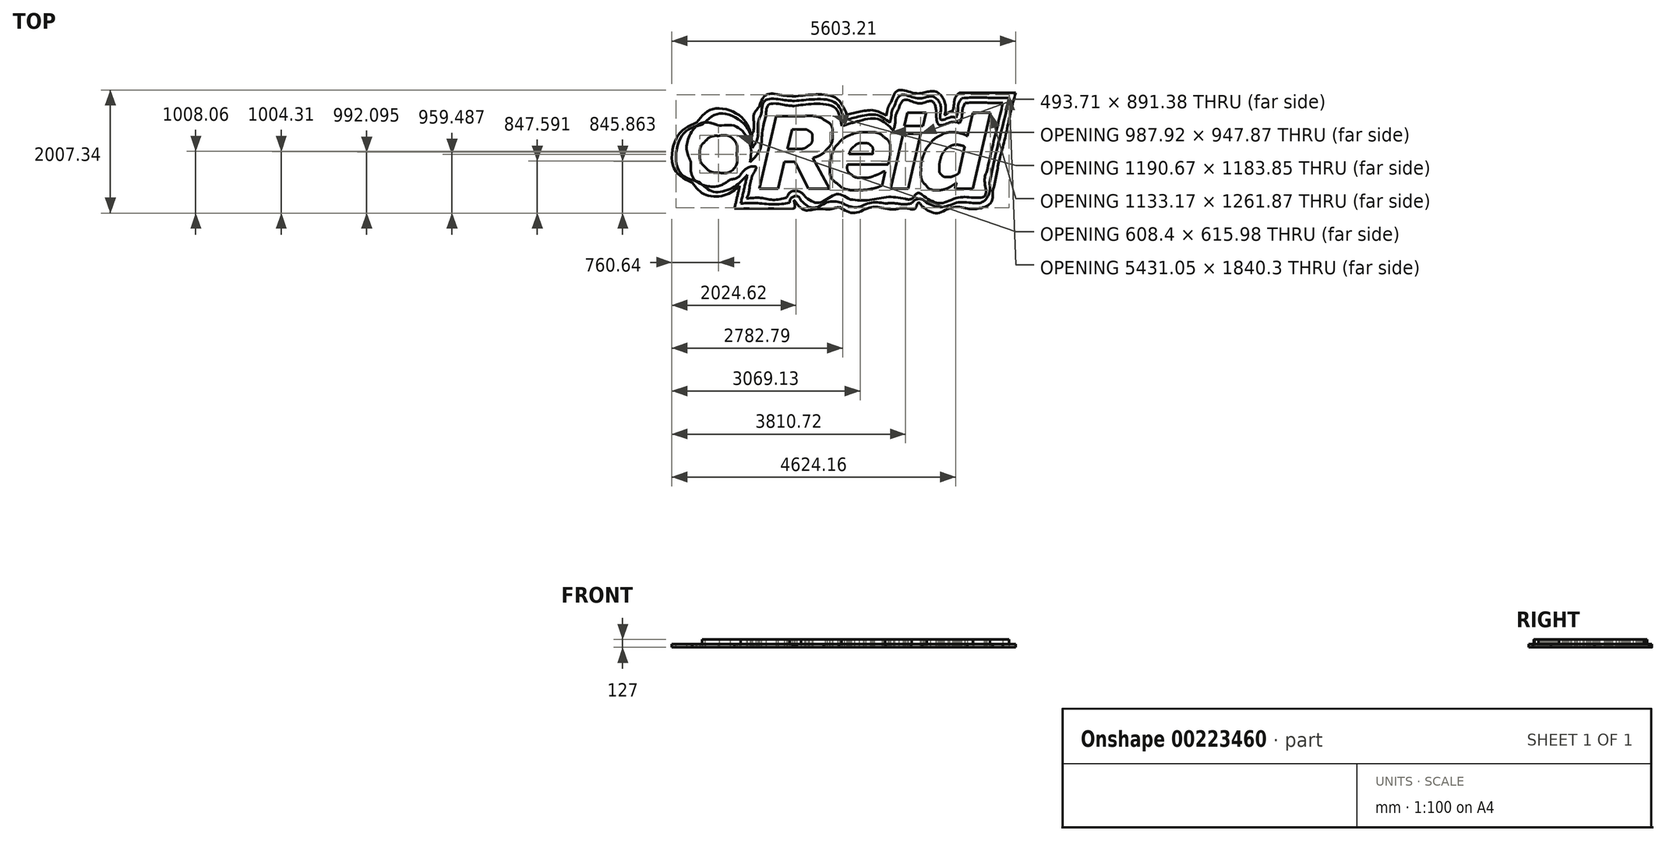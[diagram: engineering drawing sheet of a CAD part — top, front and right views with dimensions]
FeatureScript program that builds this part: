
annotation { "Feature Type Name" : "Feature", "Feature Type Description" : "" }
export const myFeature = defineFeature(function(context is Context, id is Id, definition is map)
    precondition{}
    {
        {
            var Q0;
            Q0=qCreatedBy(makeId("Top.planeOp"),FACE);
            var sketch = newSketch(context, id + "F0", { "sketchPlane" : qUnion([Q0])});
            skFitSpline(sketch, "E0", {"points": [v(-1814.54, -52.81) * mm, v(-1814.54, -217.56) * mm, v(-1948.1, -351.11) * mm, v(-2112.84, -351.11) * mm]});
            skFitSpline(sketch, "E1", {"points": [v(-2112.84, -351.11) * mm, v(-2191.95, -351.11) * mm, v(-2267.83, -319.69) * mm, v(-2323.77, -263.74) * mm]});
            skFitSpline(sketch, "E2", {"points": [v(-2323.77, -263.74) * mm, v(-2379.71, -207.8) * mm, v(-2411.14, -131.93) * mm, v(-2411.14, -52.81) * mm]});
            skFitSpline(sketch, "E3", {"points": [v(-2411.14, -52.81) * mm, v(-2411.14, 26.3) * mm, v(-2379.71, 102.18) * mm, v(-2323.77, 158.12) * mm]});
            skFitSpline(sketch, "E4", {"points": [v(-2323.77, 158.12) * mm, v(-2267.83, 214.06) * mm, v(-2191.95, 245.49) * mm, v(-2112.84, 245.49) * mm]});
            skFitSpline(sketch, "E5", {"points": [v(-2112.84, 245.49) * mm, v(-1948.1, 245.49) * mm, v(-1814.54, 111.93) * mm, v(-1814.54, -52.81) * mm]});
            skFitSpline(sketch, "E6", {"points": [v(1769.4, -519.26) * mm, v(1741.88, -536.72) * mm, v(1717.54, -552.6) * mm, v(1696.37, -566.88) * mm]});
            skFitSpline(sketch, "E7", {"points": [v(1696.37, -566.88) * mm, v(1675.74, -580.64) * mm, v(1652.72, -593.34) * mm, v(1627.32, -604.98) * mm]});
            skFitSpline(sketch, "E8", {"points": [v(1627.32, -604.98) * mm, v(1603.5, -615.57) * mm, v(1579.96, -623.5) * mm, v(1556.67, -628.8) * mm]});
            skFitSpline(sketch, "E9", {"points": [v(1556.67, -628.8) * mm, v(1533.92, -634.09) * mm, v(1506.4, -636.73) * mm, v(1474.12, -636.73) * mm]});
            skFitSpline(sketch, "E10", {"points": [v(1474.12, -636.73) * mm, v(1387.87, -636.73) * mm, v(1318.81, -608.69) * mm, v(1266.95, -552.6) * mm]});
            skFitSpline(sketch, "E11", {"points": [v(1266.95, -552.6) * mm, v(1215.63, -496.5) * mm, v(1189.96, -416.87) * mm, v(1189.96, -313.68) * mm]});
            skFitSpline(sketch, "E12", {"points": [v(1189.96, -313.68) * mm, v(1189.96, -229.01) * mm, v(1203.45, -149.64) * mm, v(1230.44, -75.55) * mm]});
            skFitSpline(sketch, "E13", {"points": [v(1230.44, -75.55) * mm, v(1257.96, -0.94) * mm, v(1295.53, 64.94) * mm, v(1343.15, 122.1) * mm]});
            skFitSpline(sketch, "E14", {"points": [v(1343.15, 122.1) * mm, v(1389.72, 177.65) * mm, v(1444.75, 221.84) * mm, v(1508.25, 254.65) * mm]});
            skFitSpline(sketch, "E15", {"points": [v(1508.25, 254.65) * mm, v(1571.75, 287.46) * mm, v(1638.16, 303.86) * mm, v(1707.49, 303.86) * mm]});
            skFitSpline(sketch, "E16", {"points": [v(1707.49, 303.86) * mm, v(1756.17, 303.86) * mm, v(1798.5, 298.83) * mm, v(1834.49, 288.78) * mm]});
            skFitSpline(sketch, "E17", {"points": [v(1834.49, 288.78) * mm, v(1870.47, 279.25) * mm, v(1907.51, 264.17) * mm, v(1945.61, 243.53) * mm]});
            skLineSegment(sketch, "E18", {"start": v(2321.05, 622.95) * mm, "end": v(2035.3, -612.13) * mm});
            skLineSegment(sketch, "E19", {"start": v(2035.3, -612.13) * mm, "end": v(1747.97, -612.13) * mm});
            skLineSegment(sketch, "E20", {"start": v(1747.97, -612.13) * mm, "end": v(1769.4, -519.26) * mm});
            skFitSpline(sketch, "E21", {"points": [v(1905.92, 71.3) * mm, v(1890.58, 78.7) * mm, v(1870.47, 85.31) * mm, v(1845.6, 91.13) * mm]});
            skFitSpline(sketch, "E22", {"points": [v(1845.6, 91.13) * mm, v(1820.73, 97.48) * mm, v(1798.77, 100.66) * mm, v(1779.72, 100.66) * mm]});
            skFitSpline(sketch, "E23", {"points": [v(1779.72, 100.66) * mm, v(1734.2, 100.66) * mm, v(1693.2, 90.6) * mm, v(1656.69, 70.5) * mm]});
            skFitSpline(sketch, "E24", {"points": [v(1656.69, 70.5) * mm, v(1620.17, 50.39) * mm, v(1589.22, 22.87) * mm, v(1563.82, -12.05) * mm]});
            skFitSpline(sketch, "E25", {"points": [v(1563.82, -12.05) * mm, v(1541.06, -43.27) * mm, v(1523.07, -83.23) * mm, v(1509.84, -131.9) * mm]});
            skFitSpline(sketch, "E26", {"points": [v(1509.84, -131.9) * mm, v(1496.61, -180.06) * mm, v(1490, -226.63) * mm, v(1490, -271.6) * mm]});
            skFitSpline(sketch, "E27", {"points": [v(1490, -271.6) * mm, v(1490, -325.05) * mm, v(1502.43, -363.95) * mm, v(1527.3, -388.3) * mm]});
            skFitSpline(sketch, "E28", {"points": [v(1527.3, -388.3) * mm, v(1552.18, -412.63) * mm, v(1590.01, -424.8) * mm, v(1640.81, -424.8) * mm]});
            skFitSpline(sketch, "E29", {"points": [v(1640.81, -424.8) * mm, v(1666.74, -424.8) * mm, v(1694, -418.98) * mm, v(1722.57, -407.34) * mm]});
            skFitSpline(sketch, "E30", {"points": [v(1722.57, -407.34) * mm, v(1751.67, -395.7) * mm, v(1779.19, -381.94) * mm, v(1805.12, -366.07) * mm]});
            skLineSegment(sketch, "E31", {"start": v(1945.61, 243.53) * mm, "end": v(2033.72, 622.95) * mm});
            skLineSegment(sketch, "E32", {"start": v(2033.72, 622.95) * mm, "end": v(2321.05, 622.95) * mm});
            skLineSegment(sketch, "E33", {"start": v(1805.12, -366.07) * mm, "end": v(1905.92, 71.3) * mm});
            skLineSegment(sketch, "E34", {"start": v(1905.92, 71.3) * mm, "end": v(1805.12, -366.07) * mm});
            skLineSegment(sketch, "E35", {"start": v(1187.9, 279.25) * mm, "end": v(981.52, -612.13) * mm});
            skLineSegment(sketch, "E36", {"start": v(981.52, -612.13) * mm, "end": v(694.18, -612.13) * mm});
            skLineSegment(sketch, "E37", {"start": v(694.18, -612.13) * mm, "end": v(900.55, 279.25) * mm});
            skLineSegment(sketch, "E38", {"start": v(900.55, 279.25) * mm, "end": v(1187.9, 279.25) * mm});
            skFitSpline(sketch, "E39", {"points": [v(402.49, -51.74) * mm, v(404.07, -42.22) * mm, v(405.13, -33.48) * mm, v(405.66, -25.55) * mm]});
            skFitSpline(sketch, "E40", {"points": [v(405.66, -25.55) * mm, v(406.72, -17.6) * mm, v(407.25, -9.4) * mm, v(407.25, -0.94) * mm]});
            skFitSpline(sketch, "E41", {"points": [v(407.25, -0.94) * mm, v(407.25, 40.86) * mm, v(394.28, 72.88) * mm, v(368.35, 95.1) * mm]});
            skFitSpline(sketch, "E42", {"points": [v(368.35, 95.1) * mm, v(342.43, 117.33) * mm, v(305.12, 128.44) * mm, v(256.44, 128.44) * mm]});
            skFitSpline(sketch, "E43", {"points": [v(256.44, 128.44) * mm, v(197.7, 128.44) * mm, v(148.22, 112.57) * mm, v(108, 80.82) * mm]});
            skFitSpline(sketch, "E44", {"points": [v(108, 80.82) * mm, v(68.32, 49.07) * mm, v(38.15, 4.88) * mm, v(17.52, -51.74) * mm]});
            skLineSegment(sketch, "E45", {"start": v(1275.2, 622.95) * mm, "end": v(1225.2, 406.25) * mm});
            skLineSegment(sketch, "E46", {"start": v(1225.2, 406.25) * mm, "end": v(921.98, 406.25) * mm});
            skLineSegment(sketch, "E47", {"start": v(921.98, 406.25) * mm, "end": v(972, 622.95) * mm});
            skLineSegment(sketch, "E48", {"start": v(972, 622.95) * mm, "end": v(1275.2, 622.95) * mm});
            skFitSpline(sketch, "E49", {"points": [v(184.2, -635.94) * mm, v(32.33, -635.94) * mm, v(-84.88, -602.34) * mm, v(-167.43, -535.13) * mm]});
            skFitSpline(sketch, "E50", {"points": [v(-167.43, -535.13) * mm, v(-249.98, -467.93) * mm, v(-291.25, -375.06) * mm, v(-291.25, -256.53) * mm]});
            skFitSpline(sketch, "E51", {"points": [v(-291.25, -256.53) * mm, v(-291.25, -175.57) * mm, v(-277.76, -101.22) * mm, v(-250.77, -33.48) * mm]});
            skFitSpline(sketch, "E52", {"points": [v(-250.77, -33.48) * mm, v(-223.78, 34.25) * mm, v(-184.89, 93.78) * mm, v(-134.09, 145.1) * mm]});
            skFitSpline(sketch, "E53", {"points": [v(-134.09, 145.1) * mm, v(-85.4, 194.85) * mm, v(-24.55, 234.27) * mm, v(48.47, 263.38) * mm]});
            skFitSpline(sketch, "E54", {"points": [v(48.47, 263.38) * mm, v(121.5, 292.48) * mm, v(201.67, 307.03) * mm, v(288.98, 307.03) * mm]});
            skFitSpline(sketch, "E55", {"points": [v(288.98, 307.03) * mm, v(421.8, 307.03) * mm, v(521.81, 280.05) * mm, v(589.02, 226.07) * mm]});
            skFitSpline(sketch, "E56", {"points": [v(589.02, 226.07) * mm, v(656.75, 172.63) * mm, v(690.62, 93.52) * mm, v(690.62, -11.26) * mm]});
            skFitSpline(sketch, "E57", {"points": [v(690.62, -11.26) * mm, v(690.62, -47.24) * mm, v(686.91, -82.43) * mm, v(679.5, -116.83) * mm]});
            skFitSpline(sketch, "E58", {"points": [v(679.5, -116.83) * mm, v(672.63, -151.22) * mm, v(663.37, -185.35) * mm, v(651.72, -219.22) * mm]});
            skLineSegment(sketch, "E59", {"start": v(17.52, -51.74) * mm, "end": v(402.49, -51.74) * mm});
            skLineSegment(sketch, "E60", {"start": v(402.49, -51.74) * mm, "end": v(402.49, -51.74) * mm});
            skLineSegment(sketch, "E61", {"start": v(402.49, -51.74) * mm, "end": v(17.52, -51.74) * mm});
            skFitSpline(sketch, "E62", {"points": [v(-10.26, -219.22) * mm, v(-10.26, -222.4) * mm, v(-10.26, -225.57) * mm, v(-10.26, -228.75) * mm]});
            skFitSpline(sketch, "E63", {"points": [v(-10.26, -228.75) * mm, v(-10.26, -231.4) * mm, v(-10.26, -234.3) * mm, v(-10.26, -237.48) * mm]});
            skFitSpline(sketch, "E64", {"points": [v(-10.26, -237.48) * mm, v(-10.26, -299.39) * mm, v(11.43, -347.8) * mm, v(54.82, -382.73) * mm]});
            skFitSpline(sketch, "E65", {"points": [v(54.82, -382.73) * mm, v(98.22, -417.66) * mm, v(164.63, -435.12) * mm, v(254.05, -435.12) * mm]});
            skFitSpline(sketch, "E66", {"points": [v(254.05, -435.12) * mm, v(316.5, -435.12) * mm, v(375.5, -424.54) * mm, v(431.06, -403.37) * mm]});
            skFitSpline(sketch, "E67", {"points": [v(431.06, -403.37) * mm, v(487.15, -382.2) * mm, v(535.84, -358.66) * mm, v(577.11, -332.73) * mm]});
            skLineSegment(sketch, "E68", {"start": v(651.72, -219.22) * mm, "end": v(-10.26, -219.22) * mm});
            skLineSegment(sketch, "E69", {"start": v(-10.26, -219.22) * mm, "end": v(651.72, -219.22) * mm});
            skFitSpline(sketch, "E70", {"points": [v(555.68, -562.12) * mm, v(500.12, -586.46) * mm, v(441.64, -604.72) * mm, v(380.26, -616.9) * mm]});
            skFitSpline(sketch, "E71", {"points": [v(380.26, -616.9) * mm, v(318.88, -629.6) * mm, v(253.53, -635.94) * mm, v(184.2, -635.94) * mm]});
            skLineSegment(sketch, "E72", {"start": v(577.11, -332.73) * mm, "end": v(608.86, -332.73) * mm});
            skLineSegment(sketch, "E73", {"start": v(608.86, -332.73) * mm, "end": v(555.68, -562.12) * mm});
            skFitSpline(sketch, "E74", {"points": [v(-252.96, 272.1) * mm, v(-252.96, 177.39) * mm, v(-281.8, 97.75) * mm, v(-339.47, 33.2) * mm]});
            skFitSpline(sketch, "E75", {"points": [v(-339.47, 33.2) * mm, v(-397.15, -31.37) * mm, v(-475.47, -80.05) * mm, v(-574.42, -112.86) * mm]});
            skFitSpline(sketch, "E76", {"points": [v(-706.19, 569.77) * mm, v(-561.72, 569.77) * mm, v(-450.07, 545.16) * mm, v(-371.22, 495.95) * mm]});
            skFitSpline(sketch, "E77", {"points": [v(-371.22, 495.95) * mm, v(-292.38, 447.26) * mm, v(-252.96, 372.65) * mm, v(-252.96, 272.1) * mm]});
            skLineSegment(sketch, "E78", {"start": v(-574.42, -112.86) * mm, "end": v(-301.37, -612.13) * mm});
            skLineSegment(sketch, "E79", {"start": v(-301.37, -612.13) * mm, "end": v(-641.9, -612.13) * mm});
            skLineSegment(sketch, "E80", {"start": v(-641.9, -612.13) * mm, "end": v(-864.14, -178.74) * mm});
            skLineSegment(sketch, "E81", {"start": v(-864.14, -178.74) * mm, "end": v(-1035.6, -178.74) * mm});
            skLineSegment(sketch, "E82", {"start": v(-1035.6, -178.74) * mm, "end": v(-1135.6, -612.13) * mm});
            skLineSegment(sketch, "E83", {"start": v(-1135.6, -612.13) * mm, "end": v(-1440.4, -612.13) * mm});
            skLineSegment(sketch, "E84", {"start": v(-1440.4, -612.13) * mm, "end": v(-1167.36, 569.77) * mm});
            skLineSegment(sketch, "E85", {"start": v(-1167.36, 569.77) * mm, "end": v(-706.19, 569.77) * mm});
            skFitSpline(sketch, "E86", {"points": [v(-581.57, 221.3) * mm, v(-581.57, 268.93) * mm, v(-596.91, 302.54) * mm, v(-627.6, 322.12) * mm]});
            skFitSpline(sketch, "E87", {"points": [v(-627.6, 322.12) * mm, v(-657.77, 342.22) * mm, v(-702.48, 352.28) * mm, v(-761.75, 352.28) * mm]});
            skFitSpline(sketch, "E88", {"points": [v(-836.36, 33.98) * mm, v(-755.4, 33.98) * mm, v(-692.7, 50.39) * mm, v(-648.24, 83.2) * mm]});
            skFitSpline(sketch, "E89", {"points": [v(-648.24, 83.2) * mm, v(-603.8, 116.54) * mm, v(-581.57, 162.57) * mm, v(-581.57, 221.3) * mm]});
            skLineSegment(sketch, "E90", {"start": v(-761.75, 352.28) * mm, "end": v(-912.56, 352.28) * mm});
            skLineSegment(sketch, "E91", {"start": v(-912.56, 352.28) * mm, "end": v(-986.38, 33.98) * mm});
            skLineSegment(sketch, "E92", {"start": v(-986.38, 33.98) * mm, "end": v(-836.36, 33.98) * mm});
            skFitSpline(sketch, "E93", {"points": [v(1275.32, 959.3) * mm, v(1083.36, 943.5) * mm, v(823.12, 989.53) * mm, v(703.26, 796) * mm]});
            skFitSpline(sketch, "E94", {"points": [v(703.26, 796) * mm, v(662.65, 728.4) * mm, v(640.58, 651.63) * mm, v(624.92, 574.9) * mm]});
            skFitSpline(sketch, "E95", {"points": [v(624.92, 574.9) * mm, v(421.51, 662.45) * mm, v(190.63, 638.72) * mm, v(-19.09, 592.52) * mm]});
            skFitSpline(sketch, "E96", {"points": [v(-19.09, 592.52) * mm, v(-194.22, 863.1) * mm, v(-550.42, 919.66) * mm, v(-848.52, 894.06) * mm]});
            skFitSpline(sketch, "E97", {"points": [v(-848.52, 894.06) * mm, v(-1053.23, 906.09) * mm, v(-1321.92, 920.88) * mm, v(-1445.5, 720.67) * mm]});
            skFitSpline(sketch, "E98", {"points": [v(-1445.5, 720.67) * mm, v(-1533.79, 583) * mm, v(-1529.5, 384.1) * mm, v(-1571.98, 255.45) * mm]});
            skFitSpline(sketch, "E99", {"points": [v(-1571.98, 255.45) * mm, v(-1741.79, 558.1) * mm, v(-2184.33, 688.1) * mm, v(-2467.53, 463.85) * mm]});
            skFitSpline(sketch, "E100", {"points": [v(-2467.53, 463.85) * mm, v(-2773.83, 245.51) * mm, v(-2840.26, -268.6) * mm, v(-2536.43, -518.18) * mm]});
            skFitSpline(sketch, "E101", {"points": [v(-2536.43, -518.18) * mm, v(-2330.11, -709.15) * mm, v(-1997.14, -715.56) * mm, v(-1764.39, -569.5) * mm]});
            skFitSpline(sketch, "E102", {"points": [v(-1764.39, -569.5) * mm, v(-1792.71, -692.09) * mm, v(-1821.03, -814.68) * mm, v(-1849.36, -937.28) * mm]});
            skFitSpline(sketch, "E103", {"points": [v(-904.48, -937.28) * mm, v(-863.92, -918.22) * mm, v(-877.4, -807.24) * mm, v(-830.66, -863.7) * mm]});
            skFitSpline(sketch, "E104", {"points": [v(-830.66, -863.7) * mm, v(-706.33, -962.68) * mm, v(-541.8, -950.39) * mm, v(-394.7, -941.72) * mm]});
            skFitSpline(sketch, "E105", {"points": [v(-394.7, -941.72) * mm, v(-308.91, -950.62) * mm, v(-220.41, -931.54) * mm, v(-140.18, -914.02) * mm]});
            skFitSpline(sketch, "E106", {"points": [v(-140.18, -914.02) * mm, v(102.74, -1009.55) * mm, v(364.65, -922.03) * mm, v(613.13, -936.72) * mm]});
            skFitSpline(sketch, "E107", {"points": [v(613.13, -936.72) * mm, v(751.78, -950.37) * mm, v(892.96, -929.34) * mm, v(1030.17, -947.91) * mm]});
            skFitSpline(sketch, "E108", {"points": [v(1030.17, -947.91) * mm, v(1095.87, -941.07) * mm, v(1149.8, -839.34) * mm, v(1211.98, -906.84) * mm]});
            skFitSpline(sketch, "E109", {"points": [v(1211.98, -906.84) * mm, v(1445.32, -1012.1) * mm, v(1703.92, -919.97) * mm, v(1948.1, -940.1) * mm]});
            skFitSpline(sketch, "E110", {"points": [v(1948.1, -940.1) * mm, v(2126.87, -937.95) * mm, v(2328.9, -846.1) * mm, v(2362.36, -652.36) * mm]});
            skFitSpline(sketch, "E111", {"points": [v(2362.36, -652.36) * mm, v(2415.66, -415.74) * mm, v(2460.55, -177.65) * mm, v(2524.6, 56.54) * mm]});
            skFitSpline(sketch, "E112", {"points": [v(2524.6, 56.54) * mm, v(2592.92, 354.02) * mm, v(2658.1, 652.8) * mm, v(2733.52, 948.04) * mm]});
            skLineSegment(sketch, "E113", {"start": v(-1849.36, -937.28) * mm, "end": v(-904.48, -937.28) * mm});
            skFitSpline(sketch, "E114", {"points": [v(1814.2, 948.04) * mm, v(1743.97, 856.85) * mm, v(1726.55, 740.13) * mm, v(1700.25, 631.41) * mm]});
            skFitSpline(sketch, "E115", {"points": [v(1700.25, 631.41) * mm, v(1660.43, 640.19) * mm, v(1581.93, 587.3) * mm, v(1594.37, 658.68) * mm]});
            skFitSpline(sketch, "E116", {"points": [v(1594.37, 658.68) * mm, v(1571.8, 815.68) * mm, v(1442.8, 963.37) * mm, v(1275.32, 959.3) * mm]});
            skLineSegment(sketch, "E117", {"start": v(2733.52, 948.04) * mm, "end": v(1814.2, 948.04) * mm});
            skFitSpline(sketch, "E118", {"points": [v(1275.6, 877.89) * mm, v(1106.32, 862.65) * mm, v(866.64, 911.86) * mm, v(763.07, 737.55) * mm]});
            skFitSpline(sketch, "E119", {"points": [v(763.07, 737.55) * mm, v(718.14, 651.42) * mm, v(704.42, 553.89) * mm, v(683.54, 460.18) * mm]});
            skFitSpline(sketch, "E120", {"points": [v(683.54, 460.18) * mm, v(457.44, 589.41) * mm, v(182.43, 561.68) * mm, v(-57.23, 501.02) * mm]});
            skFitSpline(sketch, "E121", {"points": [v(-57.23, 501.02) * mm, v(-211.3, 790.82) * mm, v(-579.88, 840.87) * mm, v(-874.4, 814.15) * mm]});
            skFitSpline(sketch, "E122", {"points": [v(-874.4, 814.15) * mm, v(-1062.75, 833.93) * mm, v(-1342.9, 826.78) * mm, v(-1410.1, 608.53) * mm]});
            skFitSpline(sketch, "E123", {"points": [v(-1410.1, 608.53) * mm, v(-1468.78, 424.14) * mm, v(-1469.3, 223.69) * mm, v(-1559.4, 48.58) * mm]});
            skFitSpline(sketch, "E124", {"points": [v(-1559.4, 48.58) * mm, v(-1645.8, 382.2) * mm, v(-2060.02, 614.17) * mm, v(-2371.05, 431.88) * mm]});
            skFitSpline(sketch, "E125", {"points": [v(-2371.05, 431.88) * mm, v(-2704.92, 251.4) * mm, v(-2762.46, -308.24) * mm, v(-2417.36, -507.96) * mm]});
            skFitSpline(sketch, "E126", {"points": [v(-2417.36, -507.96) * mm, v(-2173.67, -666.5) * mm, v(-1843.38, -575.3) * mm, v(-1639.1, -388.14) * mm]});
            skFitSpline(sketch, "E127", {"points": [v(-1639.1, -388.14) * mm, v(-1675.08, -544.04) * mm, v(-1711.09, -699.93) * mm, v(-1747.08, -855.82) * mm]});
            skFitSpline(sketch, "E128", {"points": [v(-1747.08, -855.82) * mm, v(-1483.52, -849) * mm, v(-1203.78, -870.66) * mm, v(-950.47, -844.9) * mm]});
            skFitSpline(sketch, "E129", {"points": [v(-950.47, -844.9) * mm, v(-925.6, -767.05) * mm, v(-816.35, -739.02) * mm, v(-766.17, -809.35) * mm]});
            skFitSpline(sketch, "E130", {"points": [v(-766.17, -809.35) * mm, v(-561.38, -928.12) * mm, v(-323.03, -830.85) * mm, v(-103.98, -844.15) * mm]});
            skFitSpline(sketch, "E131", {"points": [v(-103.98, -844.15) * mm, v(127.57, -917.63) * mm, v(368.4, -845.06) * mm, v(605.4, -855.23) * mm]});
            skFitSpline(sketch, "E132", {"points": [v(605.4, -855.23) * mm, v(749.6, -851.24) * mm, v(894.88, -867.05) * mm, v(1037.55, -855.78) * mm]});
            skFitSpline(sketch, "E133", {"points": [v(1037.55, -855.78) * mm, v(1105.76, -791.63) * mm, v(1212.63, -790.19) * mm, v(1284.33, -847.33) * mm]});
            skFitSpline(sketch, "E134", {"points": [v(1284.33, -847.33) * mm, v(1531.39, -915.6) * mm, v(1785.97, -841.68) * mm, v(2036.72, -850.86) * mm]});
            skFitSpline(sketch, "E135", {"points": [v(2036.72, -850.86) * mm, v(2199.24, -827.21) * mm, v(2308.88, -674.6) * mm, v(2309.26, -515.85) * mm]});
            skFitSpline(sketch, "E136", {"points": [v(2309.26, -515.85) * mm, v(2408.7, -54.02) * mm, v(2522.94, 408.25) * mm, v(2628.62, 866.1) * mm]});
            skFitSpline(sketch, "E137", {"points": [v(2628.62, 866.1) * mm, v(2370.67, 863.75) * mm, v(2110.92, 874.46) * mm, v(1854.52, 861.02) * mm]});
            skFitSpline(sketch, "E138", {"points": [v(1854.52, 861.02) * mm, v(1802.04, 761.45) * mm, v(1792.23, 647.49) * mm, v(1761.93, 540.54) * mm]});
            skFitSpline(sketch, "E139", {"points": [v(1761.93, 540.54) * mm, v(1678, 551.86) * mm, v(1518.41, 508.34) * mm, v(1511.86, 639.2) * mm]});
            skFitSpline(sketch, "E140", {"points": [v(1511.86, 639.2) * mm, v(1506.69, 758.12) * mm, v(1400.77, 882.5) * mm, v(1275.6, 877.89) * mm]});
            skFitSpline(sketch, "E141", {"points": [v(1265.6, 795.38) * mm, v(1119.68, 780.3) * mm, v(920.2, 833.62) * mm, v(827.92, 685.28) * mm]});
            skFitSpline(sketch, "E142", {"points": [v(827.92, 685.28) * mm, v(779.25, 573.53) * mm, v(770.23, 450.18) * mm, v(738.74, 333.38) * mm]});
            skFitSpline(sketch, "E143", {"points": [v(738.74, 333.38) * mm, v(498.32, 517.55) * mm, v(171.7, 486.9) * mm, v(-99.77, 406.32) * mm]});
            skFitSpline(sketch, "E144", {"points": [v(-99.77, 406.32) * mm, v(-220.1, 708.21) * mm, v(-594.47, 765.5) * mm, v(-878.76, 732.9) * mm]});
            skFitSpline(sketch, "E145", {"points": [v(-878.76, 732.9) * mm, v(-1033.48, 749.93) * mm, v(-1283.06, 757.4) * mm, v(-1337.19, 569) * mm]});
            skFitSpline(sketch, "E146", {"points": [v(-1337.19, 569) * mm, v(-1395.96, 310.3) * mm, v(-1430.03, 34.42) * mm, v(-1595.2, -184) * mm]});
            skFitSpline(sketch, "E147", {"points": [v(-1595.2, -184) * mm, v(-1593.3, 100.61) * mm, v(-1803.64, 390.04) * mm, v(-2099.03, 413.07) * mm]});
            skFitSpline(sketch, "E148", {"points": [v(-2099.03, 413.07) * mm, v(-2409.18, 446.98) * mm, v(-2626.93, 99.85) * mm, v(-2557.78, -180.3) * mm]});
            skFitSpline(sketch, "E149", {"points": [v(-2557.78, -180.3) * mm, v(-2507.1, -461.5) * mm, v(-2161.84, -579.72) * mm, v(-1920.08, -466.45) * mm]});
            skFitSpline(sketch, "E150", {"points": [v(-1920.08, -466.45) * mm, v(-1792.67, -429.35) * mm, v(-1701.86, -325.5) * mm, v(-1596.98, -256.78) * mm]});
            skFitSpline(sketch, "E151", {"points": [v(-1596.98, -256.78) * mm, v(-1494.72, -264.08) * mm, v(-1558.22, -399.8) * mm, v(-1571.43, -456.56) * mm]});
            skFitSpline(sketch, "E152", {"points": [v(-1571.43, -456.56) * mm, v(-1598.3, -560.94) * mm, v(-1612.8, -671.19) * mm, v(-1649.69, -775.77) * mm]});
            skFitSpline(sketch, "E153", {"points": [v(-1649.69, -775.77) * mm, v(-1431.55, -763.56) * mm, v(-1208.95, -795.68) * mm, v(-997.07, -761.17) * mm]});
            skFitSpline(sketch, "E154", {"points": [v(-997.07, -761.17) * mm, v(-923.58, -661.48) * mm, v(-770, -672.77) * mm, v(-690.09, -756.36) * mm]});
            skFitSpline(sketch, "E155", {"points": [v(-690.09, -756.36) * mm, v(-452.99, -842.84) * mm, v(-200.15, -708.63) * mm, v(39.8, -790.14) * mm]});
            skFitSpline(sketch, "E156", {"points": [v(39.8, -790.14) * mm, v(338.09, -801.47) * mm, v(638.14, -751.7) * mm, v(936.78, -779.5) * mm]});
            skFitSpline(sketch, "E157", {"points": [v(936.78, -779.5) * mm, v(1040.97, -777.58) * mm, v(1135.73, -685.36) * mm, v(1242.93, -738.82) * mm]});
            skFitSpline(sketch, "E158", {"points": [v(1242.93, -738.82) * mm, v(1497.11, -851.73) * mm, v(1779.83, -764.13) * mm, v(2046.35, -762.37) * mm]});
            skFitSpline(sketch, "E159", {"points": [v(2046.35, -762.37) * mm, v(2239.97, -720.38) * mm, v(2228.93, -483.92) * mm, v(2266.33, -332.41) * mm]});
            skFitSpline(sketch, "E160", {"points": [v(2266.33, -332.41) * mm, v(2349.23, 40.79) * mm, v(2439.59, 412.27) * mm, v(2526.23, 784.62) * mm]});
            skFitSpline(sketch, "E161", {"points": [v(2526.23, 784.62) * mm, v(2320.36, 784.6) * mm, v(2112.72, 790.5) * mm, v(1908.22, 782.08) * mm]});
            skFitSpline(sketch, "E162", {"points": [v(1908.22, 782.08) * mm, v(1868.3, 674.95) * mm, v(1858.05, 559.64) * mm, v(1821.14, 451.52) * mm]});
            skFitSpline(sketch, "E163", {"points": [v(1821.14, 451.52) * mm, v(1692.51, 471.93) * mm, v(1492.63, 423.25) * mm, v(1439.3, 585.75) * mm]});
            skFitSpline(sketch, "E164", {"points": [v(1439.3, 585.75) * mm, v(1434.9, 682.3) * mm, v(1382.17, 805.7) * mm, v(1265.6, 795.38) * mm]});
            skSolve(sketch);
        }
        {
            var Q0;
            Q0=makeQuery(id+"F0.imprint","IMPRINT",FACE,{"disambiguationData":[TD([[makeQuery(id+"F0.imprint","IMPRINT",EDGE,{"derivedFrom":sQuery(id+"F0.wireOp",EDGE,"E74")}),-1.0]])]});
            var Q1;
            Q1=makeQuery(id+"F0.imprint","IMPRINT",FACE,{"disambiguationData":[TD([[makeQuery(id+"F0.imprint","IMPRINT",EDGE,{"derivedFrom":sQuery(id+"F0.wireOp",EDGE,"E39")}),-1.0]])]});
            var Q2;
            Q2=makeQuery(id+"F0.imprint","IMPRINT",FACE,{"disambiguationData":[TD([[makeQuery(id+"F0.imprint","IMPRINT",EDGE,{"derivedFrom":sQuery(id+"F0.wireOp",EDGE,"E35")}),-1.0]])]});
            var Q3;
            Q3=makeQuery(id+"F0.imprint","IMPRINT",FACE,{"disambiguationData":[TD([[makeQuery(id+"F0.imprint","IMPRINT",EDGE,{"derivedFrom":sQuery(id+"F0.wireOp",EDGE,"E45")}),-1.0]])]});
            var Q4;
            Q4=makeQuery(id+"F0.imprint","IMPRINT",FACE,{"disambiguationData":[TD([[makeQuery(id+"F0.imprint","IMPRINT",EDGE,{"derivedFrom":sQuery(id+"F0.wireOp",EDGE,"E6")}),-1.0]])]});
            var Q5;
            Q5=makeQuery(id+"F0.imprint","IMPRINT",FACE,{"disambiguationData":[TD([[makeQuery(id+"F0.imprint","IMPRINT",EDGE,{"derivedFrom":sQuery(id+"F0.wireOp",EDGE,"E118")}),1.0]])]});
            extrude(context, id + "F1", {"entities" : qUnion([Q0, Q1, Q2, Q3, Q4, Q5]), "depth" : 127 * mm});
        }
        {
            var Q0;
            Q0=makeQuery(id+"F0.imprint","IMPRINT",FACE,{"disambiguationData":[TD([[makeQuery(id+"F0.imprint","IMPRINT",EDGE,{"derivedFrom":sQuery(id+"F0.wireOp",EDGE,"E93")}),1.0]])]});
            var Q1;
            Q1=makeQuery(id+"F0.imprint","IMPRINT",FACE,{"disambiguationData":[TD([[makeQuery(id+"F0.imprint","IMPRINT",EDGE,{"derivedFrom":sQuery(id+"F0.wireOp",EDGE,"E0")}),1.0]])]});
            var Q2;
            Q2=makeQuery(id+"F0.imprint","IMPRINT",FACE,{"disambiguationData":[TD([[makeQuery(id+"F0.imprint","IMPRINT",EDGE,{"derivedFrom":sQuery(id+"F0.wireOp",EDGE,"E86")}),1.0]])]});
            var Q3;
            Q3=makeQuery(id+"F0.imprint","IMPRINT",FACE,{"disambiguationData":[TD([[makeQuery(id+"F0.imprint","IMPRINT",EDGE,{"derivedFrom":sQuery(id+"F0.wireOp",EDGE,"E39")}),1.0]])]});
            var Q4;
            Q4=makeQuery(id+"F0.imprint","IMPRINT",FACE,{"disambiguationData":[TD([[makeQuery(id+"F0.imprint","IMPRINT",EDGE,{"derivedFrom":sQuery(id+"F0.wireOp",EDGE,"E21")}),1.0]])]});
            extrude(context, id + "F2", {"entities" : qUnion([Q0, Q1, Q2, Q3, Q4]), "depth" : 50.8 * mm});
        }
    });
